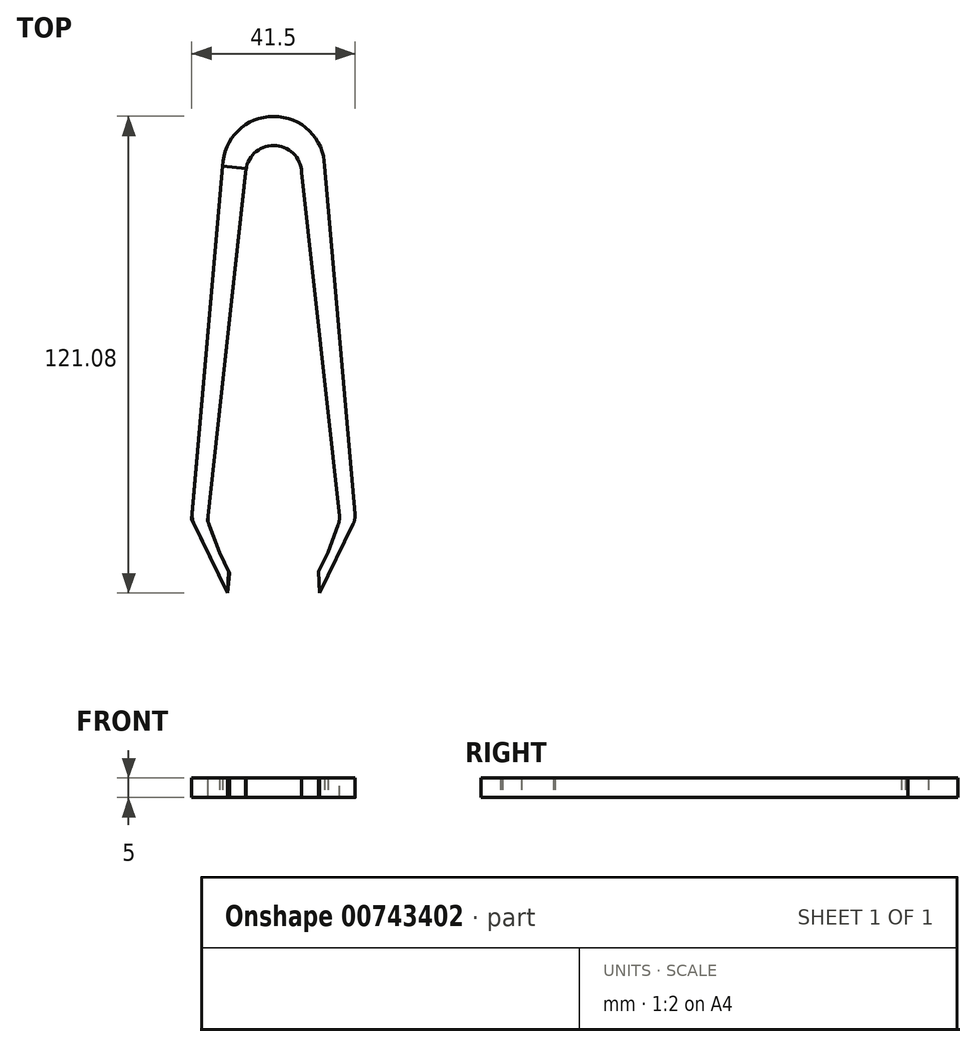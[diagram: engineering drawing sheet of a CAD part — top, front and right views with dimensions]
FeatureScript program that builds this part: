
annotation { "Feature Type Name" : "Feature", "Feature Type Description" : "" }
export const myFeature = defineFeature(function(context is Context, id is Id, definition is map)
    precondition{}
    {
        {
            var Q0;
            Q0=qCreatedBy(makeId("Top.planeOp"),FACE);
            var sketch = newSketch(context, id + "F0", { "sketchPlane" : qUnion([Q0])});
            skLineSegment(sketch, "E0", {"start": v(0, -66.28) * mm, "end": v(0, -61.28) * mm});
            skLineSegment(sketch, "E1", {"start": v(0, -61.28) * mm, "end": v(-3, -56.28) * mm});
            skLineSegment(sketch, "E2", {"start": v(0, -66.28) * mm, "end": v(-3, -61.28) * mm});
            skLineSegment(sketch, "E3", {"start": v(-3, -61.28) * mm, "end": v(-10.72, -48.42) * mm});
            skLineSegment(sketch, "E4", {"start": v(-10.72, -48.42) * mm, "end": v(-10.72, 41.58) * mm});
            skLineSegment(sketch, "E5", {"start": v(-6.72, -48.42) * mm, "end": v(-3, -56.28) * mm});
            skLineSegment(sketch, "E6", {"start": v(-10.72, 41.58) * mm, "end": v(-4.72, 41.58) * mm});
            skLineSegment(sketch, "E7", {"start": v(-4.72, 41.58) * mm, "end": v(-6.72, -48.42) * mm});
            skSolve(sketch);
        }
        {
            var Q0;
            Q0 = qSketchRegion(id + "F0", true);
            extrude(context, id + "F1", {"entities" : qUnion([Q0]), "depth" : 5 * mm, "offsetDistance" : 25 * mm});
        }
        {
            var Q0;
            Q0=makeQuery(id+"F1.opExtrude","SWEPT_BODY",BODY,{"disambiguationData":[OSD([sQuery(id+"F0.wireOp",EDGE,"E0"),sQuery(id+"F0.wireOp",EDGE,"E1"),sQuery(id+"F0.wireOp",EDGE,"E2"),sQuery(id+"F0.wireOp",EDGE,"E3"),sQuery(id+"F0.wireOp",EDGE,"E4"),sQuery(id+"F0.wireOp",EDGE,"E5"),sQuery(id+"F0.wireOp",EDGE,"E6"),sQuery(id+"F0.wireOp",EDGE,"E7")])]});
            var Q1;
            Q1=makeQuery(id+"F1.opExtrude","SWEPT_EDGE",EDGE,{"disambiguationData":[OSD([sQuery(id+"F0.wireOp",EDGE,"E6"),sQuery(id+"F0.wireOp",EDGE,"E7")])]});
            transform(context, id + "F2", {"entities" : qUnion([Q0]), "transformType" : TransformType.ROTATION, "transformAxis" : qUnion([Q1]), "angle" : 5 * degree, "makeCopy" : false});
        }
        {
            var Q0;
            Q0=qCreatedBy(makeId("Top.planeOp"),FACE);
            var sketch = newSketch(context, id + "F3", { "sketchPlane" : qUnion([Q0])});
            skPoint(sketch, "E8.0", {"position": v(-4.72, 41.58) * mm});
            skArc(sketch, "E9", {"start": v(9.35, 40.56) * mm, "mid": v(2.26, 47.4) * mm, "end": v(-4.83, 40.56) * mm});
            skPoint(sketch, "E9.second.point", {"position": v(9.24, 41.58) * mm});
            skLineSegment(sketch, "E10.0.0", {"start": v(-4.72, 41.58) * mm, "end": v(-14.55, -47.9) * mm});
            skLineSegment(sketch, "E10.0.1", {"start": v(-14.55, -47.9) * mm, "end": v(-11.54, -56.06) * mm});
            skLineSegment(sketch, "E10.0.2", {"start": v(-11.54, -56.06) * mm, "end": v(-9.2, -60.85) * mm});
            skLineSegment(sketch, "E10.0.4", {"start": v(-9.42, -66.28) * mm, "end": v(-18.54, -47.55) * mm});
            skLineSegment(sketch, "E10.0.5", {"start": v(-18.54, -47.55) * mm, "end": v(-10.7, 42.1) * mm});
            skLineSegment(sketch, "E11", {"start": v(2.26, 40.3) * mm, "end": v(2.26, 47.4) * mm, "construction": true});
            skLineSegment(sketch, "E12.MirrorCS", {"start": v(23.06, -47.55) * mm, "end": v(15.21, 42.1) * mm});
            skLineSegment(sketch, "E13.MirrorCS", {"start": v(9.24, 41.58) * mm, "end": v(19.07, -47.9) * mm});
            skLineSegment(sketch, "E14.MirrorCS", {"start": v(19.07, -47.9) * mm, "end": v(16.06, -56.06) * mm});
            skLineSegment(sketch, "E15.MirrorCS", {"start": v(13.94, -66.28) * mm, "end": v(23.06, -47.55) * mm});
            skLineSegment(sketch, "E16.MirrorCS", {"start": v(16.06, -56.06) * mm, "end": v(13.72, -60.85) * mm});
            skArc(sketch, "E17", {"start": v(15.21, 42.1) * mm, "mid": v(2.26, 54.8) * mm, "end": v(-10.7, 42.1) * mm});
            skPoint(sketch, "E17.third.point", {"position": v(0, 54.6) * mm});
            skPoint(sketch, "E18.MirrorCS.start.orphan", {"position": v(15.21, 42.1) * mm});
            skLineSegment(sketch, "E19", {"start": v(-9.2, -60.85) * mm, "end": v(-9.42, -66.28) * mm});
            skLineSegment(sketch, "E20", {"start": v(13.72, -60.85) * mm, "end": v(13.94, -66.28) * mm});
            skPoint(sketch, "E21.MirrorCS.end.orphan", {"position": v(13.94, -66.28) * mm});
            skSolve(sketch);
        }
        {
            var Q0;
            {var subQ0=sQuery(id+"F3.wireOp",EDGE,"E10.0.1");Q0=makeQuery(id+"F3.imprint","IMPRINT",FACE,{"disambiguationData":[TD([[makeQuery(id+"F3.imprint","IMPRINT",EDGE,{"derivedFrom":subQ0}),-1.0]])]});}
            extrude(context, id + "F4", {"entities" : qUnion([Q0]), "depth" : 5 * mm, "offsetDistance" : 25 * mm});
        }
        {
            var Q0;
            Q0=makeQuery(id+"F4.opExtrude","SWEPT_EDGE",EDGE,{"disambiguationData":[OSD([sQuery(id+"F3.wireOp",EDGE,"E10.0.4"),sQuery(id+"F3.wireOp",EDGE,"E10.0.5")])]});
            var Q1;
            Q1=makeQuery(id+"F4.opExtrude","SWEPT_EDGE",EDGE,{"disambiguationData":[OSD([sQuery(id+"F3.wireOp",EDGE,"E10.0.0"),sQuery(id+"F3.wireOp",EDGE,"E10.0.1")])]});
            var Q2;
            Q2=makeQuery(id+"F4.opExtrude","SWEPT_EDGE",EDGE,{"disambiguationData":[OSD([sQuery(id+"F3.wireOp",EDGE,"E13.MirrorCS"),sQuery(id+"F3.wireOp",EDGE,"E14.MirrorCS")])]});
            var Q3;
            Q3=makeQuery(id+"F4.opExtrude","SWEPT_EDGE",EDGE,{"disambiguationData":[OSD([sQuery(id+"F3.wireOp",EDGE,"E12.MirrorCS"),sQuery(id+"F3.wireOp",EDGE,"E15.MirrorCS")])]});
            fillet(context, id + "F5", {"entities" : qUnion([Q0, Q1, Q2, Q3]), "radius" : 5 * mm, "tangentPropagation" : true, "allowEdgeOverflow" : false});
        }
    });
